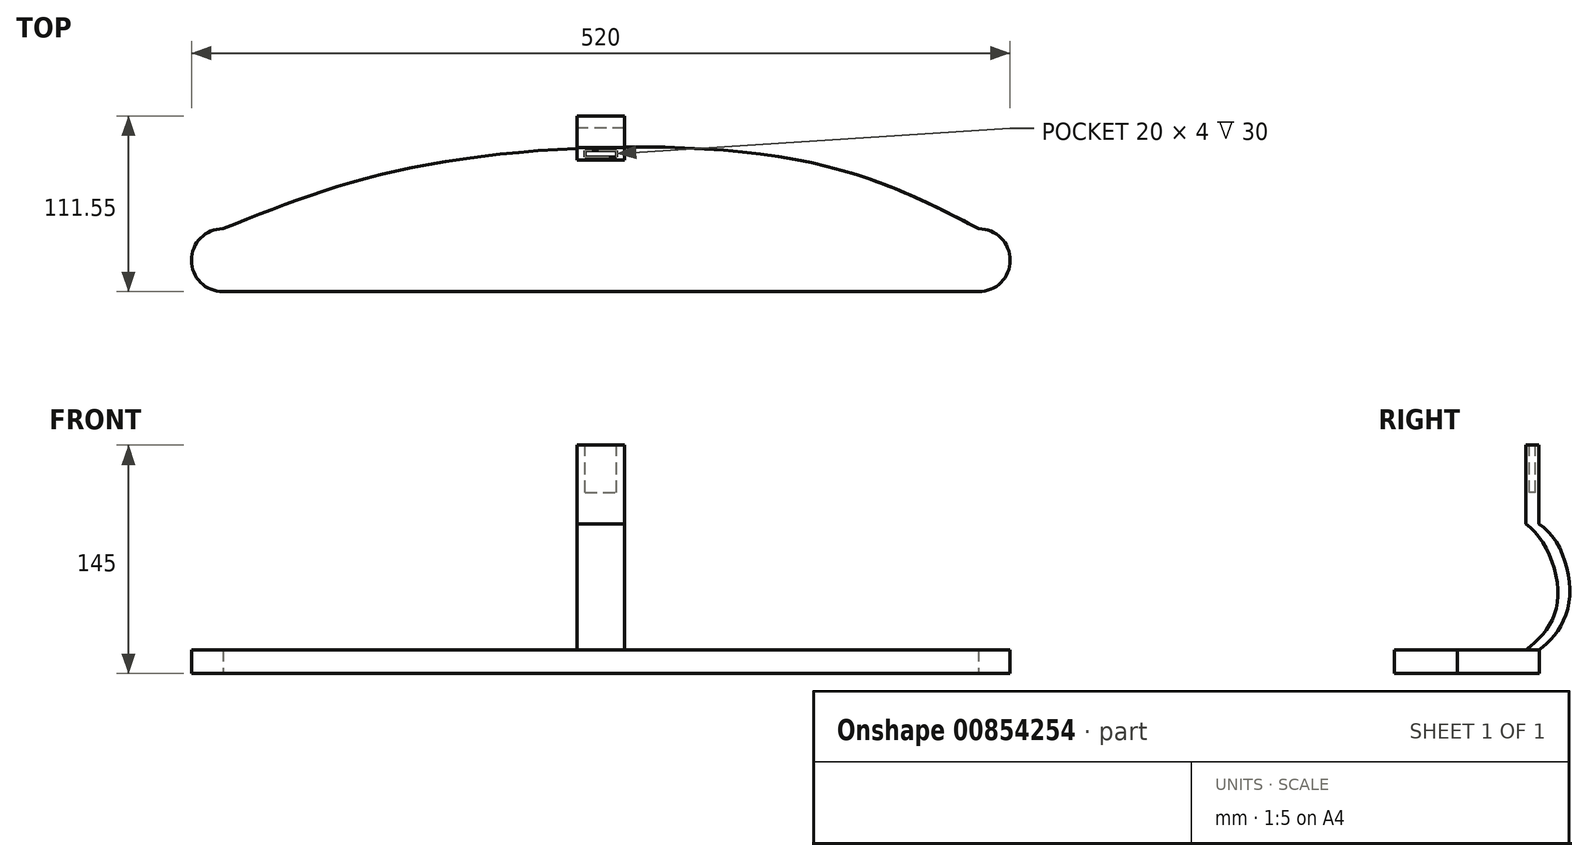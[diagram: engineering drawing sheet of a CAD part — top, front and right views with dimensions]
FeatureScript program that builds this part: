
annotation { "Feature Type Name" : "Feature", "Feature Type Description" : "" }
export const myFeature = defineFeature(function(context is Context, id is Id, definition is map)
    precondition{}
    {
        {
            var Q0;
            Q0=qCreatedBy(makeId("Top.planeOp"),FACE);
            var sketch = newSketch(context, id + "F0", { "sketchPlane" : qUnion([Q0])});
            skLineSegment(sketch, "E0.top", {"start": v(-240, -20) * mm, "end": v(240, -20) * mm});
            skArc(sketch, "E1", {"start": v(-240, 20) * mm, "mid": v(-260, 0) * mm, "end": v(-240, -20) * mm});
            skArc(sketch, "E2", {"start": v(240, -20) * mm, "mid": v(260, 0) * mm, "end": v(240, 20) * mm});
            skFitSpline(sketch, "E3", {"points": [v(-240, 20) * mm, v(-107.95, 61.04) * mm, v(124.87, 63.7) * mm, v(240, 20) * mm], "startDerivative": vector(378.86, 152.2) * mm, "endDerivative": vector(342.82, -177.87) * mm});
            skSolve(sketch);
        }
        {
            var Q0;
            Q0=makeQuery(id+"F0.imprint","IMPRINT",FACE,{"disambiguationData":[TD([[makeQuery(id+"F0.imprint","IMPRINT",EDGE,{"derivedFrom":sQuery(id+"F0.wireOp",EDGE,"E0.top")}),1.0]])]});
            extrude(context, id + "F1", {"entities" : qUnion([Q0]), "depth" : 15 * mm, "offsetDistance" : 25 * mm});
        }
        {
            var Q0;
            Q0=qCreatedBy(makeId("Right.planeOp"),FACE);
            var sketch = newSketch(context, id + "F2", { "sketchPlane" : qUnion([Q0])});
            skLineSegment(sketch, "E4.bottom", {"start": v(71.65, 15) * mm, "end": v(63.65, 15) * mm});
            skFitSpline(sketch, "E5", {"points": [v(71.65, 15) * mm, v(91.32, 47.9) * mm, v(71.65, 95) * mm], "startDerivative": vector(61.1, 40.61) * mm, "endDerivative": vector(-74.65, 45.6) * mm});
            skLineSegment(sketch, "E6", {"start": v(71.65, 95) * mm, "end": v(63.65, 95) * mm});
            skFitSpline(sketch, "E7", {"points": [v(63.65, 95) * mm, v(83.8, 47.78) * mm, v(63.65, 15) * mm], "startDerivative": vector(67.07, -45.55) * mm, "endDerivative": vector(-66.92, -49.28) * mm});
            skLineSegment(sketch, "E8.top", {"start": v(71.65, 145) * mm, "end": v(63.65, 145) * mm});
            skLineSegment(sketch, "E8.left", {"start": v(71.65, 95) * mm, "end": v(71.65, 145) * mm});
            skLineSegment(sketch, "E8.right", {"start": v(63.65, 95) * mm, "end": v(63.65, 145) * mm});
            skSolve(sketch);
        }
        {
            var Q0;
            Q0 = qSketchRegion(id + "F2", true);
            extrude(context, id + "F3", {"entities" : qUnion([Q0]), "operationType" : NewBodyOperationType.ADD, "endBound" : BoundingType.SYMMETRIC, "depth" : 30 * mm, "offsetDistance" : 25 * mm});
        }
        {
            var Q0;
            Q0=makeQuery(id+"F3.opExtrude","SWEPT_FACE",FACE,{"disambiguationData":[OSD([sQuery(id+"F2.wireOp",EDGE,"E8.top")])]});
            var sketch = newSketch(context, id + "F4", { "sketchPlane" : qUnion([Q0])});
            skPoint(sketch, "E9.oppositeSnap0", {"position": v(15, 67.65) * mm});
            skLineSegment(sketch, "E10.bottom", {"start": v(-10, 69.65) * mm, "end": v(10, 69.65) * mm});
            skLineSegment(sketch, "E10.top", {"start": v(-10, 65.65) * mm, "end": v(10, 65.65) * mm});
            skLineSegment(sketch, "E10.left", {"start": v(-10, 69.65) * mm, "end": v(-10, 65.65) * mm});
            skLineSegment(sketch, "E10.right", {"start": v(10, 69.65) * mm, "end": v(10, 65.65) * mm});
            skSolve(sketch);
        }
        {
            var Q0;
            Q0 = qSketchRegion(id + "F4", true);
            extrude(context, id + "F5", {"entities" : qUnion([Q0]), "operationType" : NewBodyOperationType.REMOVE, "oppositeDirection" : true, "depth" : 30 * mm, "offsetDistance" : 25 * mm});
        }
    });
